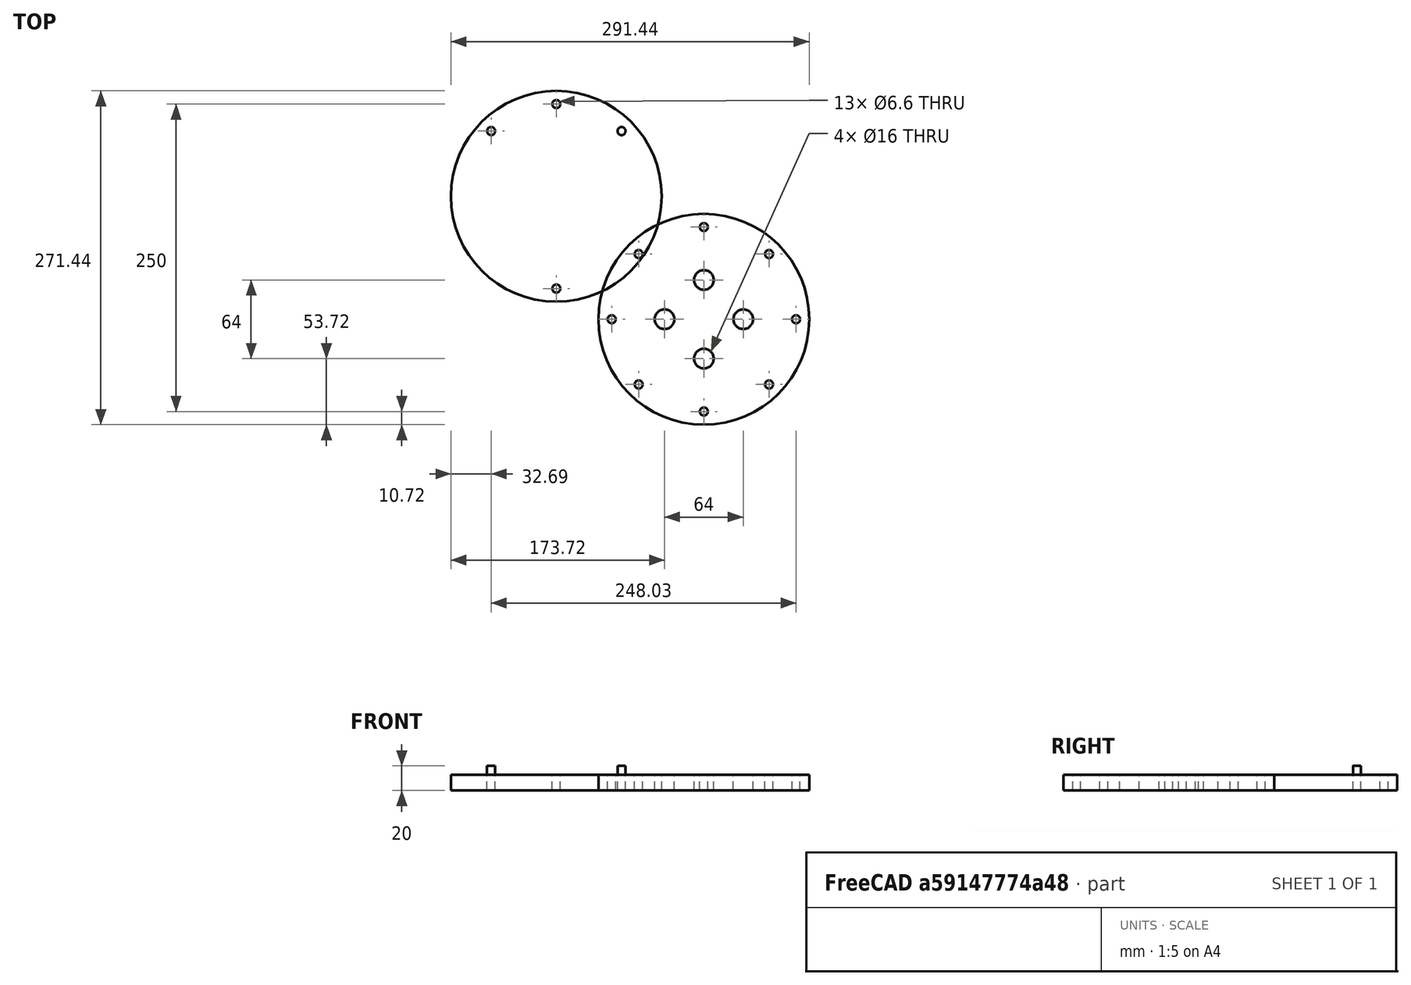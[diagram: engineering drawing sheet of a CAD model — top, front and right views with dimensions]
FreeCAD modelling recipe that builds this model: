
FCSTD DOCUMENT  (FreeCAD 0.17R13519 (Git))
Label: end plate
License: All rights reserved
LicenseURL: http://en.wikipedia.org/wiki/All_rights_reserved
objects: PartDesign::AdditiveCylinder×18, PartDesign::Body×18, Part::Cut×17, TechDraw::DrawViewDimension×5, Part::Cylinder×4, TechDraw::DrawViewPart×2, TechDraw::DrawSVGTemplate×1, TechDraw::DrawPage×1
note: 75 computed .brp shape members not serialized (recipe doc carries the construction recipe); baked Part::Feature solids carry a one-line shape summary decoded from their .brp

FEATURE [PartDesign::AdditiveCylinder] Cylinder
  Angle = 360
  AttacherType = Attacher::AttachEngine3D
  Height = 12.7
  Radius = 85.72
FEATURE [PartDesign::Body] Body
  Group = -> [Cylinder]
  Origin = -> Origin
  Tip = -> Cylinder
FEATURE [PartDesign::AdditiveCylinder] Cylinder001
  Angle = 360
  AttacherType = Attacher::AttachEngine3D
  Height = 20
  Radius = 3.3
FEATURE [PartDesign::Body] Body001
  Group = -> [Cylinder001]
  Origin = -> Origin001
  Placement = pos=(0,-75,0) rot=(0,0,1;0rad)
  Tip = -> Cylinder001
FEATURE [PartDesign::AdditiveCylinder] Cylinder002
  Angle = 360
  AttacherType = Attacher::AttachEngine3D
  Height = 20
  Radius = 3.3
FEATURE [PartDesign::Body] Body002
  Group = -> [Cylinder002]
  Origin = -> Origin002
  Placement = pos=(0,75,0) rot=(0,0,1;0rad)
  Tip = -> Cylinder002
FEATURE [PartDesign::AdditiveCylinder] Cylinder003
  Angle = 360
  AttacherType = Attacher::AttachEngine3D
  Height = 20
  Radius = 3.3
FEATURE [PartDesign::Body] Body003
  Group = -> [Cylinder003]
  Origin = -> Origin003
  Placement = pos=(75,0,0) rot=(0,0,1;0rad)
  Tip = -> Cylinder003
FEATURE [PartDesign::AdditiveCylinder] Cylinder004
  Angle = 360
  AttacherType = Attacher::AttachEngine3D
  Height = 20
  Radius = 3.3
FEATURE [PartDesign::Body] Body004
  Group = -> [Cylinder004]
  Origin = -> Origin004
  Placement = pos=(53.03,-53.03,0) rot=(0,0,1;0rad)
  Tip = -> Cylinder004
FEATURE [PartDesign::AdditiveCylinder] Cylinder005
  Angle = 360
  AttacherType = Attacher::AttachEngine3D
  Height = 20
  Radius = 3.3
FEATURE [PartDesign::Body] Body005
  Group = -> [Cylinder005]
  Origin = -> Origin005
  Placement = pos=(-75,0,0) rot=(0,0,1;0rad)
  Tip = -> Cylinder005
FEATURE [PartDesign::AdditiveCylinder] Cylinder006
  Angle = 360
  AttacherType = Attacher::AttachEngine3D
  Height = 20
  Radius = 3.3
FEATURE [PartDesign::Body] Body006
  Group = -> [Cylinder006]
  Origin = -> Origin006
  Placement = pos=(-53.03,-53.03,0) rot=(0,0,1;0rad)
  Tip = -> Cylinder006
FEATURE [PartDesign::AdditiveCylinder] Cylinder007
  Angle = 360
  AttacherType = Attacher::AttachEngine3D
  Height = 20
  Radius = 3.3
FEATURE [PartDesign::Body] Body007
  Group = -> [Cylinder007]
  Origin = -> Origin007
  Placement = pos=(53.03,53.03,0) rot=(0,0,1;0rad)
  Tip = -> Cylinder007
FEATURE [PartDesign::AdditiveCylinder] Cylinder008
  Angle = 360
  AttacherType = Attacher::AttachEngine3D
  Height = 20
  Radius = 3.3
FEATURE [PartDesign::Body] Body008
  Group = -> [Cylinder008]
  Origin = -> Origin008
  Placement = pos=(-53.03,53.03,0) rot=(0,0,1;0rad)
  Tip = -> Cylinder008
FEATURE [Part::Cut] Cut
  Base = -> Body
  Tool = -> Body001
FEATURE [Part::Cut] Cut001
  Base = -> Cut
  Tool = -> Body002
FEATURE [Part::Cut] Cut002
  Base = -> Cut001
  Tool = -> Body008
FEATURE [Part::Cut] Cut003
  Base = -> Cut002
  Tool = -> Body007
FEATURE [Part::Cut] Cut004
  Base = -> Cut003
  Tool = -> Body006
FEATURE [Part::Cut] Cut005
  Base = -> Cut004
  Tool = -> Body005
FEATURE [Part::Cut] Cut006
  Base = -> Cut005
  Tool = -> Body004
FEATURE [Part::Cut] Cut007
  Base = -> Cut006
  Tool = -> Body003
FEATURE [Part::Cylinder] Cylinder009
  Angle = 360
  AttacherType = Attacher::AttachEngine3D
  Height = 30
  Placement = pos=(-32,0,0) rot=(0,0,1;0rad)
  Radius = 8
FEATURE [Part::Cylinder] Cylinder010
  Angle = 360
  AttacherType = Attacher::AttachEngine3D
  Height = 30
  Placement = pos=(32,0,0) rot=(0,0,1;0rad)
  Radius = 8
FEATURE [Part::Cylinder] Cylinder011
  Angle = 360
  AttacherType = Attacher::AttachEngine3D
  Height = 30
  Placement = pos=(0,32,0) rot=(0,0,1;0rad)
  Radius = 8
FEATURE [Part::Cylinder] Cylinder012
  Angle = 360
  AttacherType = Attacher::AttachEngine3D
  Height = 30
  Placement = pos=(0,-32,0) rot=(0,0,1;0rad)
  Radius = 8
FEATURE [Part::Cut] Cut008
  Base = -> Cut007
  Tool = -> Cylinder010
FEATURE [Part::Cut] Cut009
  Base = -> Cut008
  Tool = -> Cylinder009
FEATURE [Part::Cut] Cut010
  Base = -> Cut009
  Tool = -> Cylinder012
FEATURE [Part::Cut] Cut011
  Base = -> Cut010
  Placement = pos=(120,-100,0) rot=(0,0,1;0rad)
  Tool = -> Cylinder011
FEATURE [PartDesign::AdditiveCylinder] Cylinder013
  Angle = 360
  AttacherType = Attacher::AttachEngine3D
  Height = 12.7
  Radius = 85.72
FEATURE [PartDesign::AdditiveCylinder] Cylinder017
  Angle = 360
  AttacherType = Attacher::AttachEngine3D
  Height = 20
  Radius = 3.3
FEATURE [PartDesign::Body] Body010
  Group = -> [Cylinder017]
  Origin = -> Origin010
  Placement = pos=(0,-75,0) rot=(0,0,1;0rad)
  Tip = -> Cylinder017
FEATURE [PartDesign::AdditiveCylinder] Cylinder019
  Angle = 360
  AttacherType = Attacher::AttachEngine3D
  Height = 20
  Radius = 3.3
FEATURE [PartDesign::AdditiveCylinder] Cylinder020
  Angle = 360
  AttacherType = Attacher::AttachEngine3D
  Height = 20
  Radius = 3.3
FEATURE [PartDesign::Body] Body012
  Group = -> [Cylinder013]
  Origin = -> Origin012
  Tip = -> Cylinder013
FEATURE [PartDesign::Body] Body013
  Group = -> [Cylinder019]
  Origin = -> Origin017
  Placement = pos=(-53.03,53.03,0) rot=(0,0,1;0rad)
  Tip = -> Cylinder019
FEATURE [PartDesign::Body] Body016
  Group = -> [Cylinder020]
  Origin = -> Origin015
  Placement = pos=(0,75,0) rot=(0,0,1;0rad)
  Tip = -> Cylinder020
FEATURE [Part::Cut] Cut022
  Base = -> Body012
  Tool = -> Body010
FEATURE [Part::Cut] Cut016
  Base = -> Cut022
  Tool = -> Body016
FEATURE [PartDesign::AdditiveCylinder] Cylinder026
  Angle = 360
  AttacherType = Attacher::AttachEngine3D
  Height = 12.7
  Radius = 85.72
FEATURE [PartDesign::AdditiveCylinder] Cylinder029
  Angle = 360
  AttacherType = Attacher::AttachEngine3D
  Height = 20
  Radius = 3.3
FEATURE [PartDesign::AdditiveCylinder] Cylinder030
  Angle = 360
  AttacherType = Attacher::AttachEngine3D
  Height = 20
  Radius = 3.3
FEATURE [PartDesign::Body] Body019
  Group = -> [Cylinder030]
  Origin = -> Origin019
  Placement = pos=(0,-75,0) rot=(0,0,1;0rad)
  Tip = -> Cylinder030
FEATURE [PartDesign::AdditiveCylinder] Cylinder032
  Angle = 360
  AttacherType = Attacher::AttachEngine3D
  Height = 20
  Radius = 3.3
FEATURE [PartDesign::AdditiveCylinder] Cylinder033
  Angle = 360
  AttacherType = Attacher::AttachEngine3D
  Height = 20
  Radius = 3.3
FEATURE [PartDesign::Body] Body021
  Group = -> [Cylinder026]
  Origin = -> Origin021
  Tip = -> Cylinder026
FEATURE [PartDesign::Body] Body022
  Group = -> [Cylinder032]
  Origin = -> Origin026
  Placement = pos=(-53.03,53.03,0) rot=(0,0,1;0rad)
  Tip = -> Cylinder032
FEATURE [PartDesign::Body] Body024
  Group = -> [Cylinder029]
  Origin = -> Origin018
  Placement = pos=(53.03,53.03,0) rot=(0,0,1;0rad)
  Tip = -> Cylinder029
FEATURE [PartDesign::Body] Body025
  Group = -> [Cylinder033]
  Origin = -> Origin024
  Placement = pos=(0,75,0) rot=(0,0,1;0rad)
  Tip = -> Cylinder033
FEATURE [Part::Cut] Cut034
  Base = -> Body021
  Tool = -> Body019
FEATURE [Part::Cut] Cut028
  Base = -> Cut034
  Tool = -> Body025
FEATURE [Part::Cut] Cut032
  Base = -> Cut028
  Tool = -> Body022
FEATURE [TechDraw::DrawSVGTemplate] Template001
  EditableTexts = Designed_by_Name=Designed by Name; Drawing_number=Drawing number; FC-Date=Date; FC-SC=Scale; FC-SH=Sheet; FC-Title=Sensor End Cap 1; Subtitle=Subtitle; Weight=Weight
  Height = 210
  Orientation = 1
  Width = 297
FEATURE [TechDraw::DrawViewPart] View
  CoarseView = false
  Direction = (0,0,1)
  Focus = 100
  HardHidden = false
  IsoCount = 0
  IsoHidden = false
  IsoVisible = false
  LockPosition = false
  Perspective = false
  Rotation = 0
  Scale = 0.8
  ScaleType = 0
  SeamHidden = false
  SeamVisible = false
  SmoothHidden = false
  SmoothVisible = false
  Source = -> [Cut011]
  X = 90
  Y = 101.994
FEATURE [TechDraw::DrawViewDimension] Dimension
  FormatSpec = %.2f
  LockPosition = false
  MeasureType = 1
  Rotation = 0
  ScaleType = 0
  Type = 4
  X = 0
  Y = 0
FEATURE [TechDraw::DrawViewPart] View001
  CoarseView = false
  Direction = (1,0,0)
  Focus = 100
  HardHidden = false
  IsoCount = 0
  IsoHidden = false
  IsoVisible = false
  LockPosition = false
  Perspective = false
  Rotation = 0
  Scale = 0.8
  ScaleType = 0
  SeamHidden = false
  SeamVisible = false
  SmoothHidden = false
  SmoothVisible = false
  Source = -> [Cut011]
  X = 90
  Y = 185
FEATURE [TechDraw::DrawViewDimension] Dimension001
  FormatSpec = %.2f
  LockPosition = false
  MeasureType = 1
  Rotation = 0
  ScaleType = 0
  Type = 4
  X = 0
  Y = 0
FEATURE [TechDraw::DrawViewDimension] Dimension002
  FormatSpec = %.2f
  LockPosition = false
  MeasureType = 1
  References2D = -> [View001]
  Rotation = 0
  ScaleType = 0
  Type = 0
  X = 58.7627
  Y = -18.8587
FEATURE [TechDraw::DrawViewDimension] Dimension003
  FormatSpec = %.2f
  LockPosition = false
  MeasureType = 1
  Rotation = 0
  ScaleType = 0
  Type = 4
  X = 0
  Y = 0
FEATURE [TechDraw::DrawViewDimension] Dimension004
  FormatSpec = %.2f
  LockPosition = false
  MeasureType = 1
  Rotation = 0
  ScaleType = 0
  Type = 4
  X = 0
  Y = 0
FEATURE [TechDraw::DrawPage] Page
  KeepUpdated = true
  ProjectionType = 0
  Template = -> Template001
  Views = -> [View,Dimension,View001,Dimension001,Dimension002,Dimension003,Dimension004]
